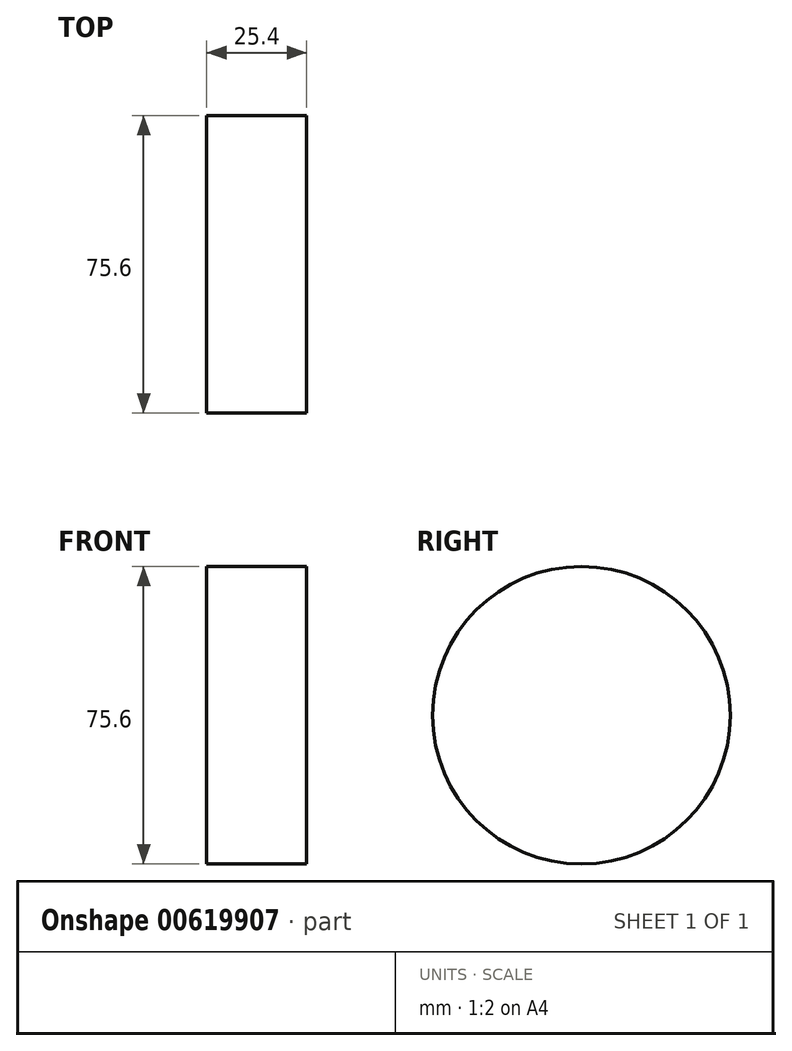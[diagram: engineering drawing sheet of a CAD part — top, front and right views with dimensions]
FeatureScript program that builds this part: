
annotation { "Feature Type Name" : "Feature", "Feature Type Description" : "" }
export const myFeature = defineFeature(function(context is Context, id is Id, definition is map)
    precondition{}
    {
        {
            var Q0;
            Q0=qCreatedBy(makeId("Right.planeOp"),FACE);
            var sketch = newSketch(context, id + "F0", { "sketchPlane" : qUnion([Q0])});
            skCircle(sketch, "E0", {"center": v(0, 0) * mm, "radius": 37.8 * mm});
            skSolve(sketch);
        }
        {
            var Q0;
            Q0=makeQuery(id+"F0.imprint","IMPRINT",FACE,{"disambiguationData":[TD([[makeQuery(id+"F0.imprint","IMPRINT",EDGE,{"derivedFrom":sQuery(id+"F0.wireOp",EDGE,"E0")}),1.0]])]});
            extrude(context, id + "F1", {"entities" : qUnion([Q0]), "depth" : 25.4 * mm, "offsetDistance" : 25.4 * mm});
        }
    });
